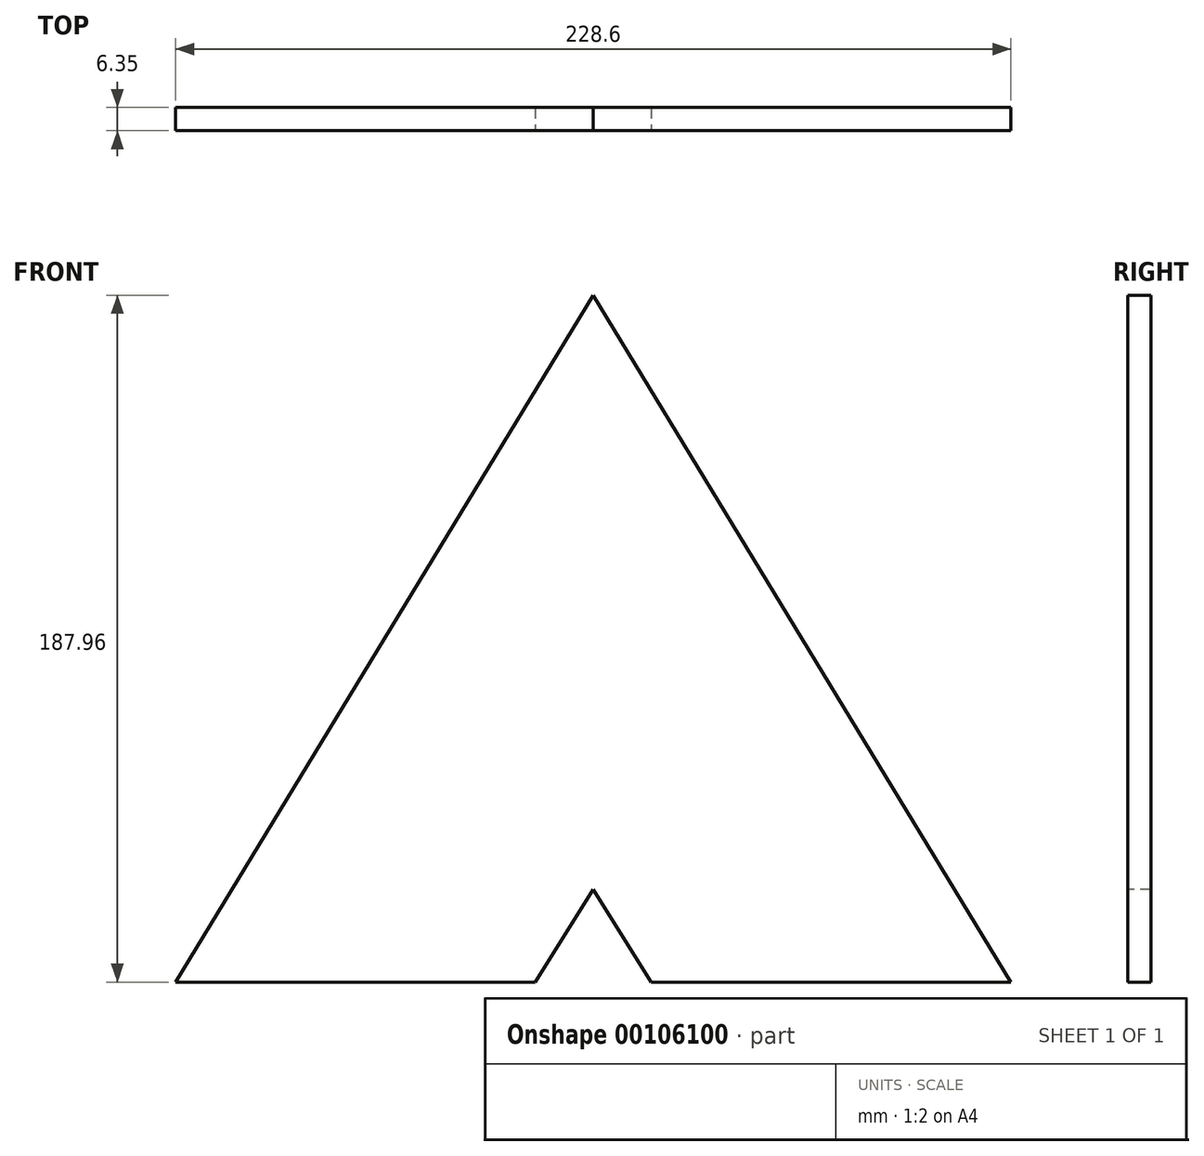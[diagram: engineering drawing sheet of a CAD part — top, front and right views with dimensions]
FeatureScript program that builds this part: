
annotation { "Feature Type Name" : "Feature", "Feature Type Description" : "" }
export const myFeature = defineFeature(function(context is Context, id is Id, definition is map)
    precondition{}
    {
        {
            var Q0;
            Q0=qCreatedBy(makeId("Front.planeOp"),FACE);
            var sketch = newSketch(context, id + "F0", { "sketchPlane" : qUnion([Q0])});
            skLineSegment(sketch, "E0", {"start": v(-114.3, 0) * mm, "end": v(114.3, 0) * mm});
            skLineSegment(sketch, "E1", {"start": v(114.3, 0) * mm, "end": v(0, 187.96) * mm});
            skLineSegment(sketch, "E2", {"start": v(0, 187.96) * mm, "end": v(-114.3, 0) * mm});
            skSolve(sketch);
        }
        {
            var Q0;
            Q0 = qSketchRegion(id + "F0", true);
            extrude(context, id + "F1", {"entities" : qUnion([Q0]), "depth" : 6.35 * mm});
        }
        {
            var Q0;
            Q0=makeQuery(id+"F1.opExtrude","CAP_FACE",FACE,{"disambiguationData":[OSD([sQuery(id+"F0.wireOp",EDGE,"E0"),sQuery(id+"F0.wireOp",EDGE,"E1"),sQuery(id+"F0.wireOp",EDGE,"E2")])],"isStart":false});
            var sketch = newSketch(context, id + "F2", { "sketchPlane" : qUnion([Q0])});
            skLineSegment(sketch, "E3", {"start": v(-15.88, 0) * mm, "end": v(0, 25.4) * mm});
            skLineSegment(sketch, "E4", {"start": v(0, 25.4) * mm, "end": v(15.88, 0) * mm});
            skLineSegment(sketch, "E5", {"start": v(15.88, 0) * mm, "end": v(-15.88, 0) * mm});
            skSolve(sketch);
        }
        {
            var Q0;
            Q0 = qSketchRegion(id + "F2", true);
            extrude(context, id + "F3", {"entities" : qUnion([Q0]), "operationType" : NewBodyOperationType.REMOVE, "endBound" : BoundingType.THROUGH_ALL, "oppositeDirection" : true, "depth" : 25.4 * mm});
        }
    });
